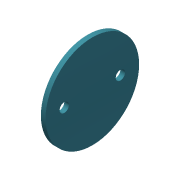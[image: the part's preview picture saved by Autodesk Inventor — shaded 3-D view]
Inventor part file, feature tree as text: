
AUTODESK INVENTOR PART (.ipt)
format: ipt  version: 2022.5 (Build 265521000, 521)  size: 90,112 bytes
history: native  units: in
note: dims shown in document units (in); Inventor stores cm internally (conversion verified against a paired STEP export)
features: extrude x1, sketch x1
ambient origin geometry x8: Origin, YZ Plane, XZ Plane, XY Plane, X Axis, Y Axis, Z Axis, Center Point
bodies: Body1 (feature_tree)
feature tree (2):
  extrude  "Extrusion16"  Depth=0.0394in
  sketch  "Sketch19"  dims[d111=0.7874in d112=0.0787in d113=0.2362in d114=0.0394in d115=0.0in]
